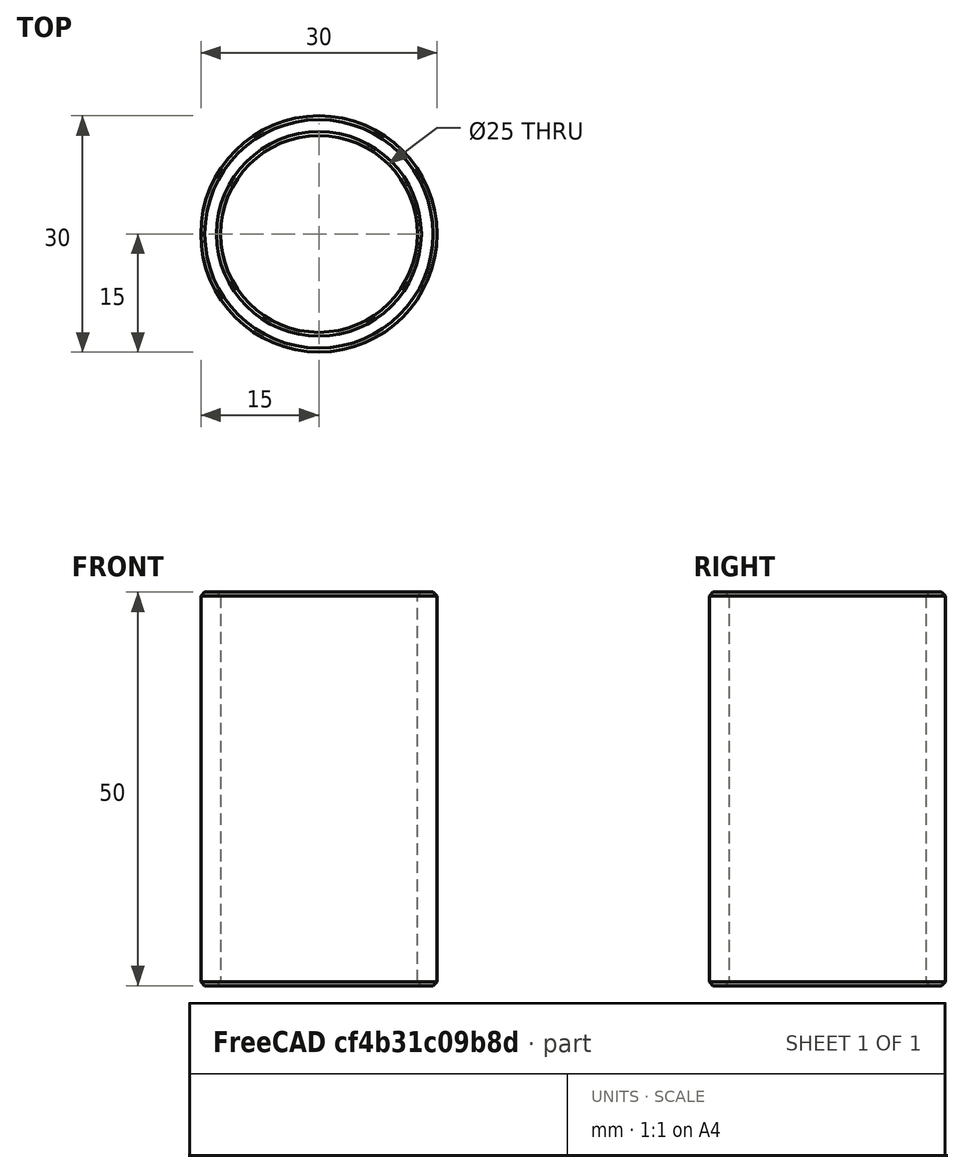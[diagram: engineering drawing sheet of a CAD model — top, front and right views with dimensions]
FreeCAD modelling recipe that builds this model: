
FCSTD DOCUMENT  (FreeCAD 0.20R29177 +426 (Git))
Label: bague
License: All rights reserved
LicenseURL: http://en.wikipedia.org/wiki/All_rights_reserved
objects: Sketcher::SketchObject×1, PartDesign::Pad×1, PartDesign::Chamfer×1, PartDesign::Body×1
note: 6 computed .brp shape members not serialized (recipe doc carries the construction recipe); baked Part::Feature solids carry a one-line shape summary decoded from their .brp

FEATURE [Sketcher::SketchObject] Sketch004
  FullyConstrained = true
  MapMode = 5
  Support = -> [XY_Plane002]
  sketch-geometry (2):
    g0: Circle CenterX=0 CenterY=0 CenterZ=0 NormalX=0 NormalY=0 NormalZ=1 AngleXU=0 Radius=12.5
    g1: Circle CenterX=0 CenterY=0 CenterZ=0 NormalX=0 NormalY=0 NormalZ=1 AngleXU=0 Radius=15
  constraints (4):
    c: Diameter(g0) = 25
    c: Coincident(g0,g-1)
    c: Diameter(g1) = 30
    c: Coincident(g1,g0)
FEATURE [PartDesign::Pad] Pad
  Direction = (0,0,1)
  Length = 50
  Length2 = 10
  Profile = -> Sketch004
  ReferenceAxis = -> Sketch004 [N_Axis]
  Type = 0
FEATURE [PartDesign::Chamfer] Chamfer
  Angle = 45
  Base = -> Pad [Edge3,Edge6,Edge2,Edge5]
  BaseFeature = -> Pad
  ChamferType = 0
  FlipDirection = false
  Size = 0.5
  Size2 = 1
  SupportTransform = false
  UseAllEdges = false
FEATURE [PartDesign::Body] Body001  label="bague"
  Group = -> [Sketch004,Pad,Chamfer]
  Origin = -> Origin002
  Placement = pos=(0,0,22) rot=(0,0,1;0rad)
  Tip = -> Chamfer
